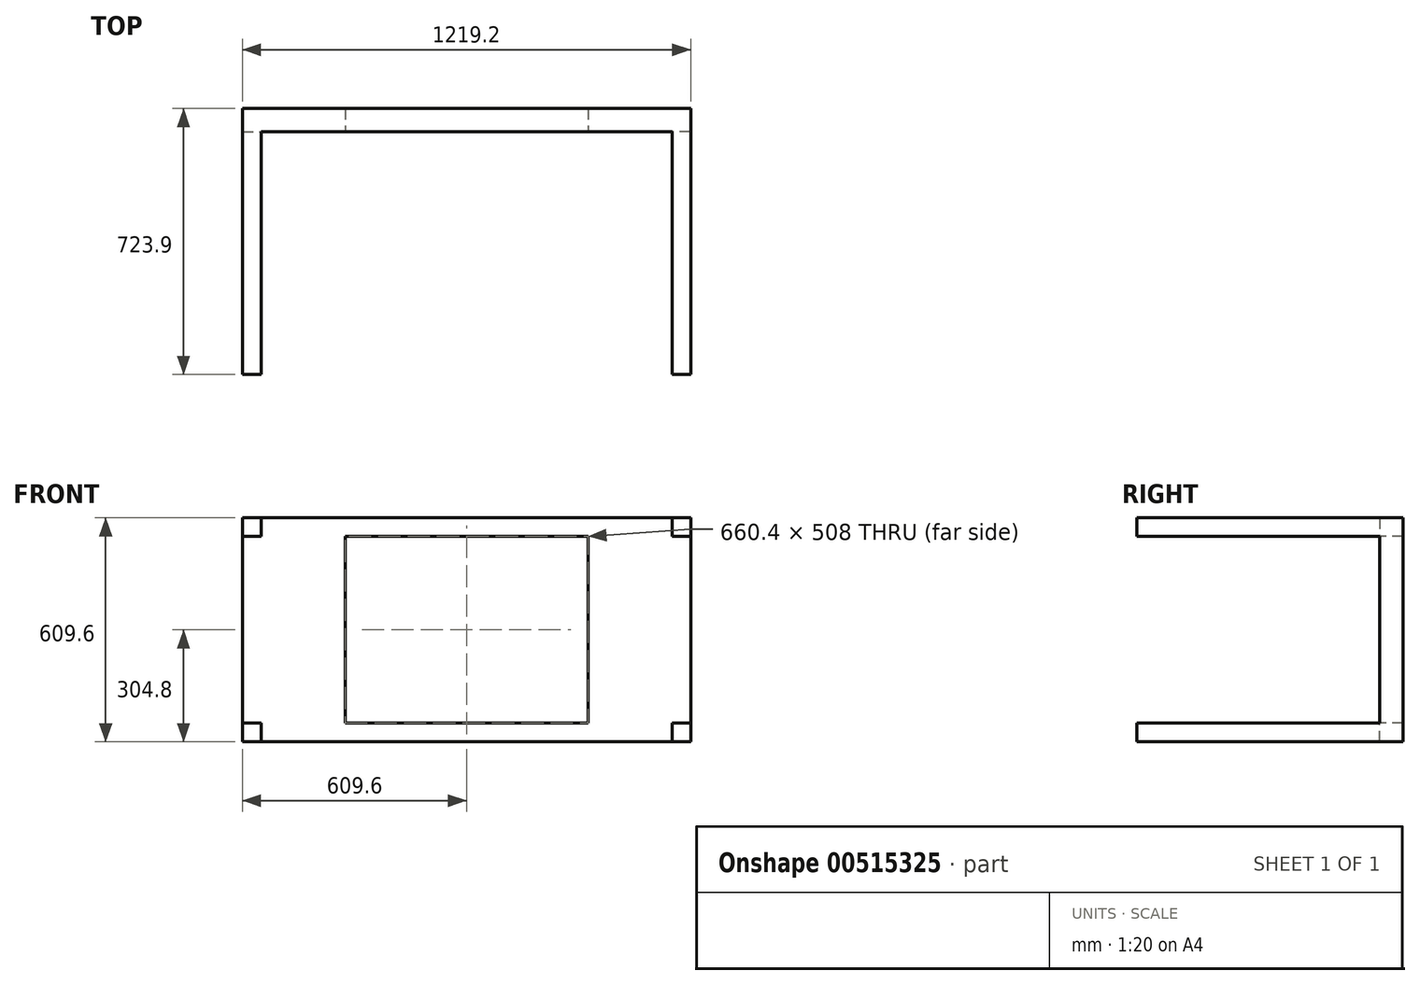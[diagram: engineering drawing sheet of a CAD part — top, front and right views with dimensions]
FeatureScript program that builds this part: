
annotation { "Feature Type Name" : "Feature", "Feature Type Description" : "" }
export const myFeature = defineFeature(function(context is Context, id is Id, definition is map)
    precondition{}
    {
        {
            var Q0;
            Q0=qCreatedBy(makeId("Front.planeOp"),FACE);
            var sketch = newSketch(context, id + "F0", { "sketchPlane" : qUnion([Q0])});
            skLineSegment(sketch, "E0.bottom", {"start": v(0, 0) * mm, "end": v(-1219.2, 0) * mm});
            skLineSegment(sketch, "E0.top", {"start": v(0, 609.6) * mm, "end": v(-1219.2, 609.6) * mm});
            skLineSegment(sketch, "E0.left", {"start": v(0, 0) * mm, "end": v(0, 609.6) * mm});
            skLineSegment(sketch, "E0.right", {"start": v(-1219.2, 0) * mm, "end": v(-1219.2, 609.6) * mm});
            skSolve(sketch);
        }
        {
            var Q0;
            Q0=makeQuery(id+"F0.imprint","IMPRINT",FACE,{"disambiguationData":[TD([[makeQuery(id+"F0.imprint","IMPRINT",EDGE,{"derivedFrom":sQuery(id+"F0.wireOp",EDGE,"E0.bottom")}),-1.0]])]});
            extrude(context, id + "F1", {"entities" : qUnion([Q0]), "depth" : 63.5 * mm, "offsetDistance" : 25.4 * mm});
        }
        {
            var Q0;
            Q0=makeQuery(id+"F1.opExtrude","CAP_FACE",FACE,{"disambiguationData":[OSD([sQuery(id+"F0.wireOp",EDGE,"E0.bottom"),sQuery(id+"F0.wireOp",EDGE,"E0.top"),sQuery(id+"F0.wireOp",EDGE,"E0.left"),sQuery(id+"F0.wireOp",EDGE,"E0.right")])],"isStart":false});
            var sketch = newSketch(context, id + "F2", { "sketchPlane" : qUnion([Q0])});
            skLineSegment(sketch, "E1", {"start": v(-1219.2, 0) * mm, "end": v(-939.8, 0) * mm});
            skLineSegment(sketch, "E2", {"start": v(-939.8, 0) * mm, "end": v(-939.8, 50.8) * mm});
            skLineSegment(sketch, "E3", {"start": v(0, 609.6) * mm, "end": v(-279.4, 609.6) * mm});
            skLineSegment(sketch, "E4", {"start": v(-279.4, 609.6) * mm, "end": v(-279.4, 558.8) * mm});
            skLineSegment(sketch, "E5.bottom", {"start": v(-939.8, 50.8) * mm, "end": v(-279.4, 50.8) * mm});
            skLineSegment(sketch, "E5.top", {"start": v(-939.8, 558.8) * mm, "end": v(-279.4, 558.8) * mm});
            skLineSegment(sketch, "E5.left", {"start": v(-939.8, 50.8) * mm, "end": v(-939.8, 558.8) * mm});
            skLineSegment(sketch, "E5.right", {"start": v(-279.4, 50.8) * mm, "end": v(-279.4, 558.8) * mm});
            skSolve(sketch);
        }
        {
            var Q0;
            Q0=makeQuery(id+"F2.imprint","IMPRINT",FACE,{"disambiguationData":[TD([[makeQuery(id+"F2.imprint","IMPRINT",EDGE,{"derivedFrom":sQuery(id+"F2.wireOp",EDGE,"E5.bottom")}),1.0]])]});
            extrude(context, id + "F3", {"entities" : qUnion([Q0]), "operationType" : NewBodyOperationType.REMOVE, "oppositeDirection" : true, "depth" : 114.3 * mm, "offsetDistance" : 25.4 * mm});
        }
        {
            var Q0;
            Q0=makeQuery(id+"F1.opExtrude","CAP_FACE",FACE,{"disambiguationData":[OSD([sQuery(id+"F0.wireOp",EDGE,"E0.bottom"),sQuery(id+"F0.wireOp",EDGE,"E0.top"),sQuery(id+"F0.wireOp",EDGE,"E0.left"),sQuery(id+"F0.wireOp",EDGE,"E0.right")])],"isStart":false});
            var sketch = newSketch(context, id + "F4", { "sketchPlane" : qUnion([Q0])});
            skLineSegment(sketch, "E6.bottom", {"start": v(-1219.2, 609.6) * mm, "end": v(-1168.4, 609.6) * mm});
            skLineSegment(sketch, "E6.top", {"start": v(-1219.2, 558.8) * mm, "end": v(-1168.4, 558.8) * mm});
            skLineSegment(sketch, "E6.left", {"start": v(-1219.2, 609.6) * mm, "end": v(-1219.2, 558.8) * mm});
            skLineSegment(sketch, "E6.right", {"start": v(-1168.4, 609.6) * mm, "end": v(-1168.4, 558.8) * mm});
            skLineSegment(sketch, "E7.bottom", {"start": v(-1219.2, 0) * mm, "end": v(-1168.4, 0) * mm});
            skLineSegment(sketch, "E7.top", {"start": v(-1219.2, 50.8) * mm, "end": v(-1168.4, 50.8) * mm});
            skLineSegment(sketch, "E7.left", {"start": v(-1219.2, 0) * mm, "end": v(-1219.2, 50.8) * mm});
            skLineSegment(sketch, "E7.right", {"start": v(-1168.4, 0) * mm, "end": v(-1168.4, 50.8) * mm});
            skLineSegment(sketch, "E8.bottom", {"start": v(0, 0) * mm, "end": v(-50.8, 0) * mm});
            skLineSegment(sketch, "E8.top", {"start": v(0, 50.8) * mm, "end": v(-50.8, 50.8) * mm});
            skLineSegment(sketch, "E8.left", {"start": v(0, 0) * mm, "end": v(0, 50.8) * mm});
            skLineSegment(sketch, "E8.right", {"start": v(-50.8, 0) * mm, "end": v(-50.8, 50.8) * mm});
            skLineSegment(sketch, "E9.bottom", {"start": v(0, 609.6) * mm, "end": v(-50.8, 609.6) * mm});
            skLineSegment(sketch, "E9.top", {"start": v(0, 558.8) * mm, "end": v(-50.8, 558.8) * mm});
            skLineSegment(sketch, "E9.left", {"start": v(0, 609.6) * mm, "end": v(0, 558.8) * mm});
            skLineSegment(sketch, "E9.right", {"start": v(-50.8, 609.6) * mm, "end": v(-50.8, 558.8) * mm});
            skSolve(sketch);
        }
        {
            var Q0;
            Q0=makeQuery(id+"F4.imprint","IMPRINT",FACE,{"disambiguationData":[TD([[makeQuery(id+"F4.imprint","IMPRINT",EDGE,{"derivedFrom":sQuery(id+"F4.wireOp",EDGE,"E6.bottom")}),1.0]])]});
            var Q1;
            Q1=makeQuery(id+"F4.imprint","IMPRINT",FACE,{"disambiguationData":[TD([[makeQuery(id+"F4.imprint","IMPRINT",EDGE,{"derivedFrom":sQuery(id+"F4.wireOp",EDGE,"E7.bottom")}),-1.0]])]});
            var Q2;
            Q2=makeQuery(id+"F4.imprint","IMPRINT",FACE,{"disambiguationData":[TD([[makeQuery(id+"F4.imprint","IMPRINT",EDGE,{"derivedFrom":sQuery(id+"F4.wireOp",EDGE,"E8.bottom")}),-1.0]])]});
            var Q3;
            Q3=makeQuery(id+"F4.imprint","IMPRINT",FACE,{"disambiguationData":[TD([[makeQuery(id+"F4.imprint","IMPRINT",EDGE,{"derivedFrom":sQuery(id+"F4.wireOp",EDGE,"E9.bottom")}),1.0]])]});
            extrude(context, id + "F5", {"entities" : qUnion([Q0, Q1, Q2, Q3]), "operationType" : NewBodyOperationType.ADD, "depth" : 660.4 * mm, "offsetDistance" : 25.4 * mm});
        }
    });
